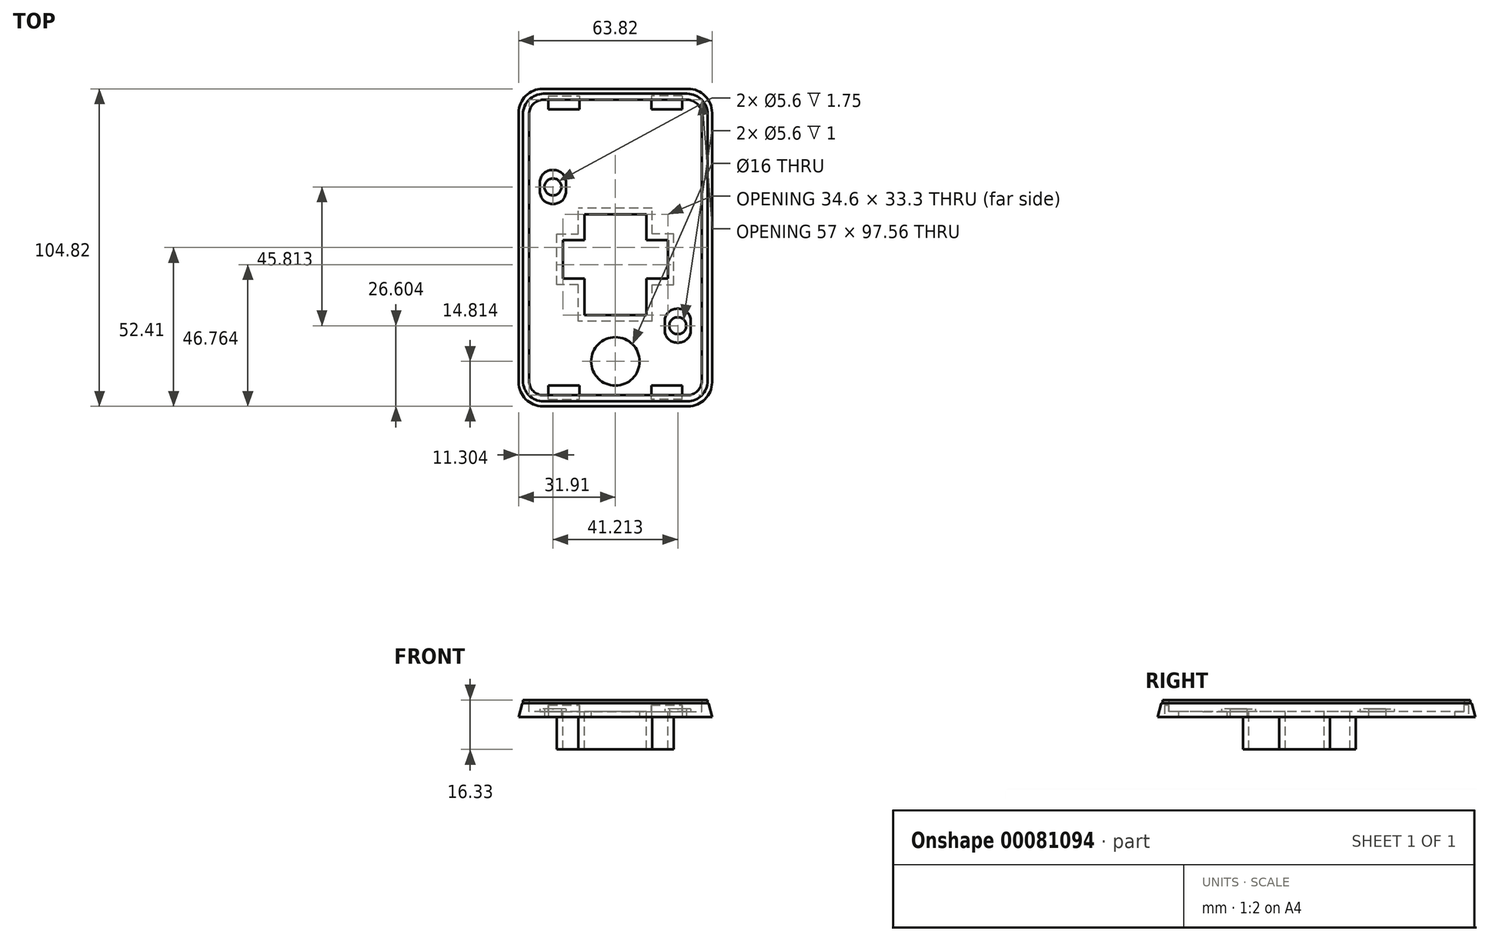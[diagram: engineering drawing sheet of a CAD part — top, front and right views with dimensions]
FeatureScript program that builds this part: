
annotation { "Feature Type Name" : "Feature", "Feature Type Description" : "" }
export const myFeature = defineFeature(function(context is Context, id is Id, definition is map)
    precondition{}
    {
        {
            var Q0;
            Q0=qCreatedBy(makeId("Top.planeOp"),FACE);
            var sketch = newSketch(context, id + "F0", { "sketchPlane" : qUnion([Q0])});
            skLineSegment(sketch, "E0", {"start": v(0, 50.78) * mm, "end": v(23.75, 50.78) * mm});
            skLineSegment(sketch, "E1", {"start": v(23.75, -50.78) * mm, "end": v(0, -50.78) * mm});
            skLineSegment(sketch, "E2", {"start": v(30.5, 44.03) * mm, "end": v(30.5, -44.03) * mm});
            skPoint(sketch, "E3.visualSharp", {"position": v(30.5, 50.78) * mm});
            skArc(sketch, "E3.filletArc", {"start": v(30.5, 44.03) * mm, "mid": v(28.52, 48.8) * mm, "end": v(23.75, 50.78) * mm});
            skPoint(sketch, "E4.visualSharp", {"position": v(30.5, -50.78) * mm});
            skArc(sketch, "E4.filletArc", {"start": v(23.75, -50.78) * mm, "mid": v(28.52, -48.8) * mm, "end": v(30.5, -44.03) * mm});
            skLineSegment(sketch, "E5.MirrorCS", {"start": v(0, 50.78) * mm, "end": v(-23.75, 50.78) * mm});
            skArc(sketch, "E6.MirrorCS", {"start": v(-30.5, 44.03) * mm, "mid": v(-28.52, 48.8) * mm, "end": v(-23.75, 50.78) * mm});
            skLineSegment(sketch, "E7.MirrorCS", {"start": v(-30.5, 44.03) * mm, "end": v(-30.5, -44.03) * mm});
            skPoint(sketch, "E8.MirrorP", {"position": v(-30.5, -50.78) * mm});
            skArc(sketch, "E9.MirrorCS", {"start": v(-23.75, -50.78) * mm, "mid": v(-28.52, -48.8) * mm, "end": v(-30.5, -44.03) * mm});
            skLineSegment(sketch, "E10.MirrorCS", {"start": v(-23.75, -50.78) * mm, "end": v(0, -50.78) * mm});
            skLineSegment(sketch, "E11.0", {"start": v(0, 48.78) * mm, "end": v(23.75, 48.78) * mm});
            skArc(sketch, "E11.1", {"start": v(28.5, 44.03) * mm, "mid": v(27.1, 47.39) * mm, "end": v(23.75, 48.78) * mm});
            skLineSegment(sketch, "E11.2", {"start": v(0, 48.78) * mm, "end": v(-23.75, 48.78) * mm});
            skLineSegment(sketch, "E11.3", {"start": v(28.5, 44.03) * mm, "end": v(28.5, -44.03) * mm});
            skArc(sketch, "E11.4", {"start": v(23.75, -48.78) * mm, "mid": v(27.1, -47.39) * mm, "end": v(28.5, -44.03) * mm});
            skLineSegment(sketch, "E11.5", {"start": v(23.75, -48.78) * mm, "end": v(0, -48.78) * mm});
            skArc(sketch, "E11.6", {"start": v(-28.5, 44.03) * mm, "mid": v(-27.1, 47.39) * mm, "end": v(-23.75, 48.78) * mm});
            skLineSegment(sketch, "E11.7", {"start": v(-28.5, 44.03) * mm, "end": v(-28.5, -44.03) * mm});
            skArc(sketch, "E11.8", {"start": v(-23.75, -48.78) * mm, "mid": v(-27.1, -47.39) * mm, "end": v(-28.5, -44.03) * mm});
            skLineSegment(sketch, "E11.9", {"start": v(-23.75, -48.78) * mm, "end": v(0, -48.78) * mm});
            skSolve(sketch);
        }
        {
            var Q0;
            Q0=makeQuery(id+"F0.imprint","IMPRINT",FACE,{"disambiguationData":[TD([[makeQuery(id+"F0.imprint","IMPRINT",EDGE,{"derivedFrom":sQuery(id+"F0.wireOp",EDGE,"E0")}),-1.0]])]});
            extrude(context, id + "F1", {"entities" : qUnion([Q0]), "depth" : 1 * mm});
        }
        {
            var Q0;
            Q0=makeQuery(id+"F1.opExtrude","CAP_FACE",FACE,{"disambiguationData":[OSD([sQuery(id+"F0.wireOp",EDGE,"E0"),sQuery(id+"F0.wireOp",EDGE,"E1"),sQuery(id+"F0.wireOp",EDGE,"E2"),sQuery(id+"F0.wireOp",EDGE,"E3.filletArc"),sQuery(id+"F0.wireOp",EDGE,"E4.filletArc"),sQuery(id+"F0.wireOp",EDGE,"E5.MirrorCS"),sQuery(id+"F0.wireOp",EDGE,"E6.MirrorCS"),sQuery(id+"F0.wireOp",EDGE,"E7.MirrorCS"),sQuery(id+"F0.wireOp",EDGE,"E9.MirrorCS"),sQuery(id+"F0.wireOp",EDGE,"E10.MirrorCS"),sQuery(id+"F0.wireOp",EDGE,"E11.0"),sQuery(id+"F0.wireOp",EDGE,"E11.1"),sQuery(id+"F0.wireOp",EDGE,"E11.2"),sQuery(id+"F0.wireOp",EDGE,"E11.3"),sQuery(id+"F0.wireOp",EDGE,"E11.4"),sQuery(id+"F0.wireOp",EDGE,"E11.5"),sQuery(id+"F0.wireOp",EDGE,"E11.6"),sQuery(id+"F0.wireOp",EDGE,"E11.7"),sQuery(id+"F0.wireOp",EDGE,"E11.8"),sQuery(id+"F0.wireOp",EDGE,"E11.9")])],"isStart":true});
            cPlane(context, id + "F2", {"entities" : qUnion([Q0]), "cplaneType" : CPlaneType.OFFSET, "offset" : (5.24 - .6) * mm, "width" : 150 * mm, "height" : 150 * mm});
        }
        {
            var Q0;
            Q0=qCreatedBy(id+"F2.planeOp",FACE);
            var sketch = newSketch(context, id + "F3", { "sketchPlane" : qUnion([Q0])});
            skLineSegment(sketch, "E12", {"start": v(0, 52.5) * mm, "end": v(24, 52.5) * mm});
            skLineSegment(sketch, "E13", {"start": v(32, 44.5) * mm, "end": v(32, 0) * mm});
            skPoint(sketch, "E14.visualSharp", {"position": v(32, 52.5) * mm});
            skArc(sketch, "E14.filletArc", {"start": v(32, 44.5) * mm, "mid": v(29.66, 50.16) * mm, "end": v(24, 52.5) * mm});
            skLineSegment(sketch, "E15.MirrorCS", {"start": v(0, 52.5) * mm, "end": v(-24, 52.5) * mm});
            skArc(sketch, "E16.MirrorCS", {"start": v(-32, 44.5) * mm, "mid": v(-29.66, 50.16) * mm, "end": v(-24, 52.5) * mm});
            skLineSegment(sketch, "E17.MirrorCS", {"start": v(-32, 44.5) * mm, "end": v(-32, 0) * mm});
            skLineSegment(sketch, "E18.MirrorCS", {"start": v(32, -44.5) * mm, "end": v(32, 0) * mm});
            skArc(sketch, "E19.MirrorCS", {"start": v(32, -44.5) * mm, "mid": v(29.66, -50.16) * mm, "end": v(24, -52.5) * mm});
            skLineSegment(sketch, "E20.MirrorCS", {"start": v(0, -52.5) * mm, "end": v(24, -52.5) * mm});
            skLineSegment(sketch, "E21.MirrorCS", {"start": v(0, -52.5) * mm, "end": v(-24, -52.5) * mm});
            skArc(sketch, "E22.MirrorCS", {"start": v(-32, -44.5) * mm, "mid": v(-29.66, -50.16) * mm, "end": v(-24, -52.5) * mm});
            skLineSegment(sketch, "E23.MirrorCS", {"start": v(-32, -44.5) * mm, "end": v(-32, 0) * mm});
            skSolve(sketch);
        }
        {
            var Q0;
            Q0=makeQuery(id+"F3.imprint","IMPRINT",FACE,{"disambiguationData":[TD([[makeQuery(id+"F3.imprint","IMPRINT",EDGE,{"derivedFrom":sQuery(id+"F3.wireOp",EDGE,"E12")}),-1.0]])]});
            var Q1;
            Q1=makeQuery(id+"F1.opExtrude","CAP_FACE",FACE,{"disambiguationData":[OSD([sQuery(id+"F0.wireOp",EDGE,"E0"),sQuery(id+"F0.wireOp",EDGE,"E1"),sQuery(id+"F0.wireOp",EDGE,"E2"),sQuery(id+"F0.wireOp",EDGE,"E3.filletArc"),sQuery(id+"F0.wireOp",EDGE,"E4.filletArc"),sQuery(id+"F0.wireOp",EDGE,"E5.MirrorCS"),sQuery(id+"F0.wireOp",EDGE,"E6.MirrorCS"),sQuery(id+"F0.wireOp",EDGE,"E7.MirrorCS"),sQuery(id+"F0.wireOp",EDGE,"E9.MirrorCS"),sQuery(id+"F0.wireOp",EDGE,"E10.MirrorCS"),sQuery(id+"F0.wireOp",EDGE,"E11.0"),sQuery(id+"F0.wireOp",EDGE,"E11.1"),sQuery(id+"F0.wireOp",EDGE,"E11.2"),sQuery(id+"F0.wireOp",EDGE,"E11.3"),sQuery(id+"F0.wireOp",EDGE,"E11.4"),sQuery(id+"F0.wireOp",EDGE,"E11.5"),sQuery(id+"F0.wireOp",EDGE,"E11.6"),sQuery(id+"F0.wireOp",EDGE,"E11.7"),sQuery(id+"F0.wireOp",EDGE,"E11.8"),sQuery(id+"F0.wireOp",EDGE,"E11.9")])],"isStart":true});
            extrude(context, id + "F4", {"entities" : qUnion([Q0]), "endBound" : BoundingType.UP_TO_SURFACE, "oppositeDirection" : true, "endBoundEntityFace" : qUnion([Q1]), "depth" : 2 * mm});
        }
        {
            var Q0;
            Q0=makeQuery(id+"F4.opExtrude","CAP_EDGE",EDGE,{"disambiguationData":[OSD([sQuery(id+"F3.wireOp",EDGE,"E20.MirrorCS"),sQuery(id+"F3.wireOp",EDGE,"E21.MirrorCS")])],"isStart":false});
            chamfer(context, id + "F5", {"entities" : qUnion([Q0]), "chamferType" : ChamferType.TWO_OFFSETS, "width1" : 1.3 * mm, "oppositeDirection" : false, "width2" : 5 * mm, "tangentPropagation" : true});
        }
        {
            var Q0;
            Q0=qCreatedBy(makeId("Top.planeOp"),FACE);
            var sketch = newSketch(context, id + "F6", { "sketchPlane" : qUnion([Q0])});
            skLineSegment(sketch, "E24.0", {"start": v(0, 48.78) * mm, "end": v(23.75, 48.78) * mm});
            skArc(sketch, "E24.1", {"start": v(28.5, 44.03) * mm, "mid": v(27.1, 47.39) * mm, "end": v(23.75, 48.78) * mm});
            skLineSegment(sketch, "E24.2", {"start": v(0, 48.78) * mm, "end": v(-23.75, 48.78) * mm});
            skLineSegment(sketch, "E24.3", {"start": v(28.5, 44.03) * mm, "end": v(28.5, -44.03) * mm});
            skArc(sketch, "E24.4", {"start": v(23.75, -48.78) * mm, "mid": v(27.1, -47.39) * mm, "end": v(28.5, -44.03) * mm});
            skLineSegment(sketch, "E24.5", {"start": v(23.75, -48.78) * mm, "end": v(0, -48.78) * mm});
            skArc(sketch, "E24.6", {"start": v(-28.5, 44.03) * mm, "mid": v(-27.1, 47.39) * mm, "end": v(-23.75, 48.78) * mm});
            skLineSegment(sketch, "E24.7", {"start": v(-28.5, 44.03) * mm, "end": v(-28.5, -44.03) * mm});
            skArc(sketch, "E24.8", {"start": v(-23.75, -48.78) * mm, "mid": v(-27.1, -47.39) * mm, "end": v(-28.5, -44.03) * mm});
            skLineSegment(sketch, "E24.9", {"start": v(-23.75, -48.78) * mm, "end": v(0, -48.78) * mm});
            skSolve(sketch);
        }
        {
            var Q0;
            Q0=makeQuery(id+"F6.imprint","IMPRINT",FACE,{"disambiguationData":[TD([[makeQuery(id+"F6.imprint","IMPRINT",EDGE,{"derivedFrom":sQuery(id+"F6.wireOp",EDGE,"E24.0")}),-1.0]])]});
            extrude(context, id + "F7", {"entities" : qUnion([Q0]), "operationType" : NewBodyOperationType.REMOVE, "oppositeDirection" : true, "depth" : (3.72 - 0.83) * mm});
        }
        {
            var Q0;
            {var subQ0=sQuery(id+"F3.wireOp",EDGE,"E15.MirrorCS");var subQ1=sQuery(id+"F3.wireOp",EDGE,"E12");Q0=makeQuery(id+"F5.opChamfer","BLEND_EDGE",EDGE,{"blendedFrom":[makeQuery(id+"F4.opExtrude","CAP_EDGE",EDGE,{"disambiguationData":[OSD([subQ1,subQ0])],"isStart":false}),makeQuery(id+"F4.opExtrude","CAP_FACE",FACE,{"disambiguationData":[OSD([subQ1,sQuery(id+"F3.wireOp",EDGE,"E13"),sQuery(id+"F3.wireOp",EDGE,"E14.filletArc"),subQ0,sQuery(id+"F3.wireOp",EDGE,"E16.MirrorCS"),sQuery(id+"F3.wireOp",EDGE,"E17.MirrorCS"),sQuery(id+"F3.wireOp",EDGE,"E18.MirrorCS"),sQuery(id+"F3.wireOp",EDGE,"E19.MirrorCS"),sQuery(id+"F3.wireOp",EDGE,"E20.MirrorCS"),sQuery(id+"F3.wireOp",EDGE,"E21.MirrorCS"),sQuery(id+"F3.wireOp",EDGE,"E22.MirrorCS"),sQuery(id+"F3.wireOp",EDGE,"E23.MirrorCS")])],"isStart":false})],"blendedInto":[makeQuery(id+"F4.opExtrude","CAP_FACE",FACE,{"disambiguationData":[OSD([subQ1,sQuery(id+"F3.wireOp",EDGE,"E13"),sQuery(id+"F3.wireOp",EDGE,"E14.filletArc"),subQ0,sQuery(id+"F3.wireOp",EDGE,"E16.MirrorCS"),sQuery(id+"F3.wireOp",EDGE,"E17.MirrorCS"),sQuery(id+"F3.wireOp",EDGE,"E18.MirrorCS"),sQuery(id+"F3.wireOp",EDGE,"E19.MirrorCS"),sQuery(id+"F3.wireOp",EDGE,"E20.MirrorCS"),sQuery(id+"F3.wireOp",EDGE,"E21.MirrorCS"),sQuery(id+"F3.wireOp",EDGE,"E22.MirrorCS"),sQuery(id+"F3.wireOp",EDGE,"E23.MirrorCS")])],"isStart":false})]});}
            fillet(context, id + "F8", {"entities" : qUnion([Q0]), "radius" : 0.4 * mm, "tangentPropagation" : true, "allowEdgeOverflow" : false});
        }
        {
            var Q0;
            Q0=makeQuery(id+"F4.opExtrude","CAP_FACE",FACE,{"disambiguationData":[OSD([sQuery(id+"F3.wireOp",EDGE,"E12"),sQuery(id+"F3.wireOp",EDGE,"E13"),sQuery(id+"F3.wireOp",EDGE,"E14.filletArc"),sQuery(id+"F3.wireOp",EDGE,"E15.MirrorCS"),sQuery(id+"F3.wireOp",EDGE,"E16.MirrorCS"),sQuery(id+"F3.wireOp",EDGE,"E17.MirrorCS"),sQuery(id+"F3.wireOp",EDGE,"E18.MirrorCS"),sQuery(id+"F3.wireOp",EDGE,"E19.MirrorCS"),sQuery(id+"F3.wireOp",EDGE,"E20.MirrorCS"),sQuery(id+"F3.wireOp",EDGE,"E21.MirrorCS"),sQuery(id+"F3.wireOp",EDGE,"E22.MirrorCS"),sQuery(id+"F3.wireOp",EDGE,"E23.MirrorCS")])],"isStart":true});
            var sketch = newSketch(context, id + "F9", { "sketchPlane" : qUnion([Q0])});
            skLineSegment(sketch, "E25.bottom", {"start": v(-22.1, 50.1) * mm, "end": v(-11.86, 50.1) * mm});
            skLineSegment(sketch, "E25.top", {"start": v(-22.1, 45.6) * mm, "end": v(-11.86, 45.6) * mm});
            skLineSegment(sketch, "E25.left", {"start": v(-22.1, 50.1) * mm, "end": v(-22.1, 45.6) * mm});
            skLineSegment(sketch, "E25.right", {"start": v(-11.86, 50.1) * mm, "end": v(-11.86, 45.6) * mm});
            skLineSegment(sketch, "E26.MirrorCS", {"start": v(22.1, 50.1) * mm, "end": v(11.86, 50.1) * mm});
            skLineSegment(sketch, "E27.MirrorCS", {"start": v(22.1, 50.1) * mm, "end": v(22.1, 45.6) * mm});
            skLineSegment(sketch, "E28.MirrorCS", {"start": v(22.1, 45.6) * mm, "end": v(11.86, 45.6) * mm});
            skLineSegment(sketch, "E29.MirrorCS", {"start": v(11.86, 50.1) * mm, "end": v(11.86, 45.6) * mm});
            skLineSegment(sketch, "E30.MirrorCS", {"start": v(-22.1, -50.1) * mm, "end": v(-22.1, -45.6) * mm});
            skLineSegment(sketch, "E31.MirrorCS", {"start": v(-22.1, -50.1) * mm, "end": v(-11.86, -50.1) * mm});
            skLineSegment(sketch, "E32.MirrorCS", {"start": v(-22.1, -45.6) * mm, "end": v(-11.86, -45.6) * mm});
            skLineSegment(sketch, "E33.MirrorCS", {"start": v(-11.86, -50.1) * mm, "end": v(-11.86, -45.6) * mm});
            skLineSegment(sketch, "E34.MirrorCS", {"start": v(11.86, -50.1) * mm, "end": v(11.86, -45.6) * mm});
            skLineSegment(sketch, "E35.MirrorCS", {"start": v(22.1, -45.6) * mm, "end": v(11.86, -45.6) * mm});
            skLineSegment(sketch, "E36.MirrorCS", {"start": v(22.1, -50.1) * mm, "end": v(11.86, -50.1) * mm});
            skLineSegment(sketch, "E37.MirrorCS", {"start": v(22.1, -50.1) * mm, "end": v(22.1, -45.6) * mm});
            skCircle(sketch, "E38", {"center": v(0, 37.6) * mm, "radius": 8 * mm});
            skCircle(sketch, "E39", {"center": v(20.6, 25.8) * mm, "radius": 2.8 * mm});
            skCircle(sketch, "E40", {"center": v(-20.6, -20) * mm, "radius": 2.8 * mm});
            skSolve(sketch);
        }
        {
            var Q0;
            Q0 = qSketchRegion(id + "F9", true);
            extrude(context, id + "F10", {"entities" : qUnion([Q0]), "operationType" : NewBodyOperationType.REMOVE, "oppositeDirection" : true, "depth" : 4 * mm});
        }
        {
            var Q0;
            Q0=makeQuery(id+"F7.boolean.opBoolean","COPY",FACE,{"derivedFrom":makeQuery(id+"F7.opExtrude","CAP_FACE",FACE,{"disambiguationData":[OSD([sQuery(id+"F6.wireOp",EDGE,"E24.0"),sQuery(id+"F6.wireOp",EDGE,"E24.1"),sQuery(id+"F6.wireOp",EDGE,"E24.2"),sQuery(id+"F6.wireOp",EDGE,"E24.3"),sQuery(id+"F6.wireOp",EDGE,"E24.4"),sQuery(id+"F6.wireOp",EDGE,"E24.5"),sQuery(id+"F6.wireOp",EDGE,"E24.6"),sQuery(id+"F6.wireOp",EDGE,"E24.7"),sQuery(id+"F6.wireOp",EDGE,"E24.8"),sQuery(id+"F6.wireOp",EDGE,"E24.9")])],"isStart":false})});
            var sketch = newSketch(context, id + "F11", { "sketchPlane" : qUnion([Q0])});
            skLineSegment(sketch, "E41.bottom", {"start": v(20.36, -20.2) * mm, "end": v(20.86, -20.2) * mm});
            skLineSegment(sketch, "E41.top", {"start": v(20.36, -31.4) * mm, "end": v(20.86, -31.4) * mm});
            skLineSegment(sketch, "E41.left", {"start": v(16.3, -24.26) * mm, "end": v(16.3, -27.36) * mm});
            skLineSegment(sketch, "E41.right", {"start": v(24.9, -24.26) * mm, "end": v(24.9, -27.36) * mm});
            skPoint(sketch, "E42.visualSharp", {"position": v(16.3, -20.2) * mm});
            skArc(sketch, "E42.filletArc", {"start": v(20.36, -20.2) * mm, "mid": v(17.5, -21.4) * mm, "end": v(16.3, -24.26) * mm});
            skPoint(sketch, "E43.visualSharp", {"position": v(24.9, -20.2) * mm});
            skArc(sketch, "E43.filletArc", {"start": v(24.9, -24.26) * mm, "mid": v(23.72, -21.4) * mm, "end": v(20.86, -20.2) * mm});
            skPoint(sketch, "E44.visualSharp", {"position": v(24.9, -31.4) * mm});
            skArc(sketch, "E44.filletArc", {"start": v(20.86, -31.4) * mm, "mid": v(23.72, -30.22) * mm, "end": v(24.9, -27.36) * mm});
            skPoint(sketch, "E45.visualSharp", {"position": v(16.3, -31.4) * mm});
            skArc(sketch, "E45.filletArc", {"start": v(16.3, -27.36) * mm, "mid": v(17.5, -30.22) * mm, "end": v(20.36, -31.4) * mm});
            skCircle(sketch, "E46", {"center": v(20.6, -25.8) * mm, "radius": 2.8 * mm});
            skLineSegment(sketch, "E47.bottom", {"start": v(-20.86, 25.6) * mm, "end": v(-20.36, 25.6) * mm});
            skLineSegment(sketch, "E47.top", {"start": v(-20.86, 14.4) * mm, "end": v(-20.36, 14.4) * mm});
            skLineSegment(sketch, "E47.left", {"start": v(-24.9, 21.56) * mm, "end": v(-24.9, 18.46) * mm});
            skLineSegment(sketch, "E47.right", {"start": v(-16.3, 21.56) * mm, "end": v(-16.3, 18.46) * mm});
            skCircle(sketch, "E48", {"center": v(-20.6, 20) * mm, "radius": 2.8 * mm});
            skPoint(sketch, "E49.visualSharp", {"position": v(-24.9, 25.6) * mm});
            skArc(sketch, "E49.filletArc", {"start": v(-20.86, 25.6) * mm, "mid": v(-23.72, 24.42) * mm, "end": v(-24.9, 21.56) * mm});
            skPoint(sketch, "E50.visualSharp", {"position": v(-16.3, 25.6) * mm});
            skArc(sketch, "E50.filletArc", {"start": v(-16.3, 21.56) * mm, "mid": v(-17.5, 24.42) * mm, "end": v(-20.36, 25.6) * mm});
            skPoint(sketch, "E51.visualSharp", {"position": v(-16.3, 14.4) * mm});
            skArc(sketch, "E51.filletArc", {"start": v(-20.36, 14.4) * mm, "mid": v(-17.5, 15.6) * mm, "end": v(-16.3, 18.46) * mm});
            skPoint(sketch, "E52.visualSharp", {"position": v(-24.9, 14.4) * mm});
            skArc(sketch, "E52.filletArc", {"start": v(-24.9, 18.46) * mm, "mid": v(-23.72, 15.6) * mm, "end": v(-20.86, 14.4) * mm});
            skSolve(sketch);
        }
        {
            var Q0;
            Q0 = qSketchRegion(id + "F11", true);
            extrude(context, id + "F12", {"entities" : qUnion([Q0]), "operationType" : NewBodyOperationType.ADD, "depth" : 1 * mm});
        }
        {
            var Q0;
            Q0=makeQuery(id+"F7.boolean.opBoolean","COPY",FACE,{"derivedFrom":makeQuery(id+"F7.opExtrude","CAP_FACE",FACE,{"disambiguationData":[OSD([sQuery(id+"F6.wireOp",EDGE,"E24.0"),sQuery(id+"F6.wireOp",EDGE,"E24.1"),sQuery(id+"F6.wireOp",EDGE,"E24.2"),sQuery(id+"F6.wireOp",EDGE,"E24.3"),sQuery(id+"F6.wireOp",EDGE,"E24.4"),sQuery(id+"F6.wireOp",EDGE,"E24.5"),sQuery(id+"F6.wireOp",EDGE,"E24.6"),sQuery(id+"F6.wireOp",EDGE,"E24.7"),sQuery(id+"F6.wireOp",EDGE,"E24.8"),sQuery(id+"F6.wireOp",EDGE,"E24.9")])],"isStart":false})});
            var sketch = newSketch(context, id + "F13", { "sketchPlane" : qUnion([Q0])});
            skLineSegment(sketch, "E53", {"start": v(0, -22.3) * mm, "end": v(-10.2, -22.3) * mm});
            skLineSegment(sketch, "E54", {"start": v(-10.2, -22.3) * mm, "end": v(-10.2, -10.3) * mm});
            skLineSegment(sketch, "E55", {"start": v(-10.2, -10.3) * mm, "end": v(-17.3, -10.3) * mm});
            skLineSegment(sketch, "E56", {"start": v(-17.3, -10.3) * mm, "end": v(-17.3, 2.5) * mm});
            skLineSegment(sketch, "E57", {"start": v(-17.3, 2.5) * mm, "end": v(-10.2, 2.5) * mm});
            skLineSegment(sketch, "E58", {"start": v(-10.2, 2.5) * mm, "end": v(-10.2, 11) * mm});
            skLineSegment(sketch, "E59", {"start": v(-10.2, 11) * mm, "end": v(0, 11) * mm});
            skLineSegment(sketch, "E60.MirrorCS", {"start": v(10.2, 11) * mm, "end": v(0, 11) * mm});
            skLineSegment(sketch, "E61.MirrorCS", {"start": v(10.2, 2.5) * mm, "end": v(10.2, 11) * mm});
            skLineSegment(sketch, "E62.MirrorCS", {"start": v(17.3, 2.5) * mm, "end": v(10.2, 2.5) * mm});
            skLineSegment(sketch, "E63.MirrorCS", {"start": v(17.3, -10.3) * mm, "end": v(17.3, 2.5) * mm});
            skLineSegment(sketch, "E64.MirrorCS", {"start": v(10.2, -10.3) * mm, "end": v(17.3, -10.3) * mm});
            skLineSegment(sketch, "E65.MirrorCS", {"start": v(10.2, -22.3) * mm, "end": v(10.2, -10.3) * mm});
            skLineSegment(sketch, "E66.MirrorCS", {"start": v(0, -22.3) * mm, "end": v(10.2, -22.3) * mm});
            skLineSegment(sketch, "E67", {"start": v(0, 13) * mm, "end": v(-12.2, 13) * mm});
            skLineSegment(sketch, "E68", {"start": v(-12.2, 13) * mm, "end": v(-12.2, 4.5) * mm});
            skLineSegment(sketch, "E69", {"start": v(-12.2, 4.5) * mm, "end": v(-19.3, 4.5) * mm});
            skLineSegment(sketch, "E70", {"start": v(-19.3, 4.5) * mm, "end": v(-19.3, -12.3) * mm});
            skLineSegment(sketch, "E71", {"start": v(-19.3, -12.3) * mm, "end": v(-12.2, -12.3) * mm});
            skLineSegment(sketch, "E72", {"start": v(-12.2, -12.3) * mm, "end": v(-12.2, -24.3) * mm});
            skLineSegment(sketch, "E73", {"start": v(-12.2, -24.3) * mm, "end": v(0, -24.3) * mm});
            skLineSegment(sketch, "E74.MirrorCS", {"start": v(0, 13) * mm, "end": v(12.2, 13) * mm});
            skLineSegment(sketch, "E75.MirrorCS", {"start": v(12.2, 13) * mm, "end": v(12.2, 4.5) * mm});
            skLineSegment(sketch, "E76.MirrorCS", {"start": v(12.2, 4.5) * mm, "end": v(19.3, 4.5) * mm});
            skLineSegment(sketch, "E77.MirrorCS", {"start": v(19.3, 4.5) * mm, "end": v(19.3, -12.3) * mm});
            skLineSegment(sketch, "E78.MirrorCS", {"start": v(19.3, -12.3) * mm, "end": v(12.2, -12.3) * mm});
            skLineSegment(sketch, "E79.MirrorCS", {"start": v(12.2, -12.3) * mm, "end": v(12.2, -24.3) * mm});
            skLineSegment(sketch, "E80.MirrorCS", {"start": v(12.2, -24.3) * mm, "end": v(0, -24.3) * mm});
            skSolve(sketch);
        }
        {
            var Q0;
            Q0 = qSketchRegion(id + "F13", true);
            extrude(context, id + "F14", {"entities" : qUnion([Q0]), "operationType" : NewBodyOperationType.ADD, "oppositeDirection" : true, "depth" : 12.44 * mm});
        }
        {
            var Q0;
            Q0=makeQuery(id+"F14.boolean.opBoolean","SPLIT",FACE,{"disambiguationData":[TD([makeQuery(id+"F14.opExtrude","SWEPT_FACE",FACE,{"disambiguationData":[OSD([sQuery(id+"F13.wireOp",EDGE,"E54")])]})])],"derivedFrom":makeQuery(id+"F4.opExtrude","CAP_FACE",FACE,{"disambiguationData":[OSD([sQuery(id+"F3.wireOp",EDGE,"E12"),sQuery(id+"F3.wireOp",EDGE,"E13"),sQuery(id+"F3.wireOp",EDGE,"E14.filletArc"),sQuery(id+"F3.wireOp",EDGE,"E15.MirrorCS"),sQuery(id+"F3.wireOp",EDGE,"E16.MirrorCS"),sQuery(id+"F3.wireOp",EDGE,"E17.MirrorCS"),sQuery(id+"F3.wireOp",EDGE,"E18.MirrorCS"),sQuery(id+"F3.wireOp",EDGE,"E19.MirrorCS"),sQuery(id+"F3.wireOp",EDGE,"E20.MirrorCS"),sQuery(id+"F3.wireOp",EDGE,"E21.MirrorCS"),sQuery(id+"F3.wireOp",EDGE,"E22.MirrorCS"),sQuery(id+"F3.wireOp",EDGE,"E23.MirrorCS")])],"isStart":true})});
            var sketch = newSketch(context, id + "F15", { "sketchPlane" : qUnion([Q0])});
            skLineSegment(sketch, "E81", {"start": v(-10.2, 22.3) * mm, "end": v(10.2, 22.3) * mm});
            skLineSegment(sketch, "E82", {"start": v(10.2, 22.3) * mm, "end": v(10.2, 10.3) * mm});
            skLineSegment(sketch, "E83", {"start": v(10.2, 10.3) * mm, "end": v(17.3, 10.3) * mm});
            skLineSegment(sketch, "E84", {"start": v(17.3, 10.3) * mm, "end": v(17.3, -2.5) * mm});
            skLineSegment(sketch, "E85", {"start": v(17.3, -2.5) * mm, "end": v(10.2, -2.5) * mm});
            skLineSegment(sketch, "E86", {"start": v(10.2, -2.5) * mm, "end": v(10.2, -11) * mm});
            skLineSegment(sketch, "E87", {"start": v(10.2, -11) * mm, "end": v(-10.2, -11) * mm});
            skLineSegment(sketch, "E88", {"start": v(-10.2, -11) * mm, "end": v(-10.2, -2.5) * mm});
            skLineSegment(sketch, "E89", {"start": v(-10.2, -2.5) * mm, "end": v(-17.3, -2.5) * mm});
            skLineSegment(sketch, "E90", {"start": v(-17.3, -2.5) * mm, "end": v(-17.3, 10.3) * mm});
            skLineSegment(sketch, "E91", {"start": v(-17.3, 10.3) * mm, "end": v(-10.2, 10.3) * mm});
            skLineSegment(sketch, "E92", {"start": v(-10.2, 10.3) * mm, "end": v(-10.2, 22.3) * mm});
            skSolve(sketch);
        }
        {
            var Q0;
            Q0=makeQuery(id+"F15.imprint","IMPRINT",FACE,{"disambiguationData":[TD([[makeQuery(id+"F15.imprint","IMPRINT",EDGE,{"derivedFrom":sQuery(id+"F15.wireOp",EDGE,"E81")}),1.0]])]});
            var Q1;
            Q1 = qSketchRegion(id + "F15", true);
            extrude(context, id + "F16", {"entities" : qUnion([Q0, Q1]), "operationType" : NewBodyOperationType.REMOVE, "endBound" : BoundingType.UP_TO_NEXT, "oppositeDirection" : true, "depth" : 25 * mm});
        }
    });
